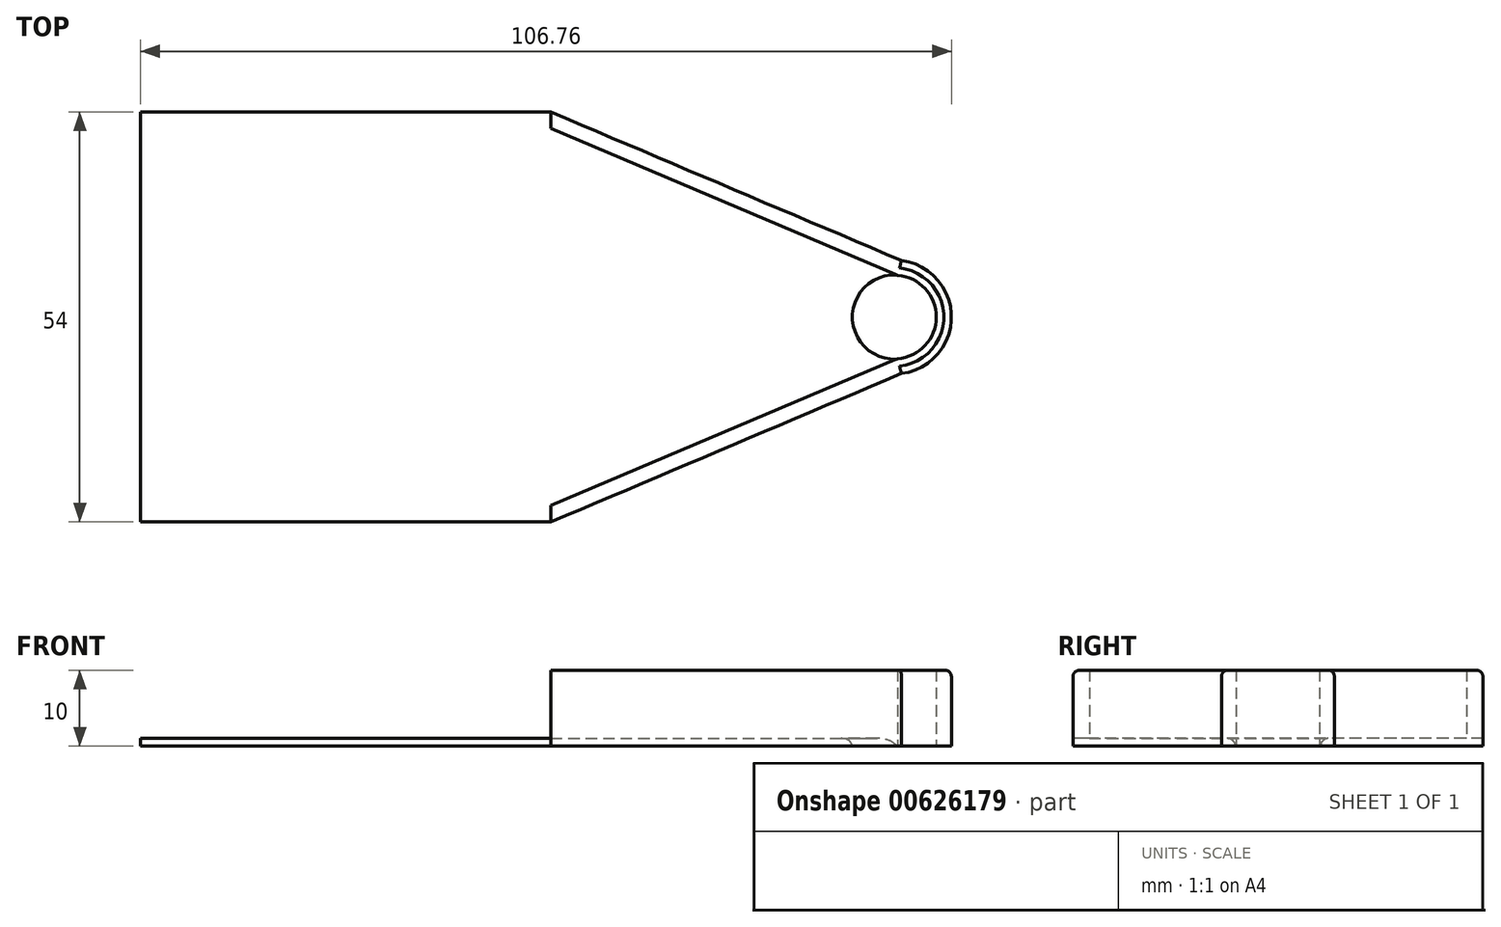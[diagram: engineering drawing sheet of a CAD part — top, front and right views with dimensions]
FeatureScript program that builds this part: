
annotation { "Feature Type Name" : "Feature", "Feature Type Description" : "" }
export const myFeature = defineFeature(function(context is Context, id is Id, definition is map)
    precondition{}
    {
        {
            var Q0;
            Q0=qCreatedBy(makeId("Top.planeOp"),FACE);
            var sketch = newSketch(context, id + "F0", { "sketchPlane" : qUnion([Q0])});
            skArc(sketch, "E0", {"start": v(12.3, -13.43) * mm, "mid": v(17.4, -7.95) * mm, "end": v(12.31, -2.46) * mm});
            skArc(sketch, "E1.3", {"start": v(12.81, -15.38) * mm, "mid": v(19.4, -7.94) * mm, "end": v(12.81, -0.5) * mm});
            skCircle(sketch, "E2", {"center": v(11.9, -7.94) * mm, "radius": 5.5 * mm});
            skLineSegment(sketch, "E3", {"start": v(-33.37, 19.06) * mm, "end": v(12.81, -0.5) * mm});
            skLineSegment(sketch, "E4", {"start": v(-33.37, -34.94) * mm, "end": v(12.81, -15.38) * mm});
            skLineSegment(sketch, "E5.0", {"start": v(-31.37, 16.04) * mm, "end": v(12.03, -2.34) * mm});
            skLineSegment(sketch, "E5.1", {"start": v(-31.37, -7.94) * mm, "end": v(-31.37, 16.04) * mm});
            skLineSegment(sketch, "E5.2", {"start": v(-31.37, -7.94) * mm, "end": v(-31.37, -31.92) * mm});
            skLineSegment(sketch, "E5.3", {"start": v(-31.37, -31.92) * mm, "end": v(12.03, -13.54) * mm});
            skLineSegment(sketch, "E6", {"start": v(12.03, -2.34) * mm, "end": v(12.31, -2.46) * mm});
            skLineSegment(sketch, "E7", {"start": v(12.03, -13.54) * mm, "end": v(12.3, -13.43) * mm});
            skLineSegment(sketch, "E8", {"start": v(-33.37, 19.06) * mm, "end": v(-33.37, -34.94) * mm});
            skLineSegment(sketch, "E9", {"start": v(-31.37, 16.04) * mm, "end": v(-33.37, 16.89) * mm});
            skLineSegment(sketch, "E10", {"start": v(-31.37, -31.92) * mm, "end": v(-33.37, -32.77) * mm});
            skLineSegment(sketch, "E11.bottom", {"start": v(-33.37, 19.06) * mm, "end": v(-87.37, 19.06) * mm});
            skLineSegment(sketch, "E11.top", {"start": v(-33.37, -34.94) * mm, "end": v(-87.37, -34.94) * mm});
            skLineSegment(sketch, "E11.right", {"start": v(-87.37, 19.06) * mm, "end": v(-87.37, -34.94) * mm});
            skSolve(sketch);
        }
        {
            var Q0;
            Q0=makeQuery(id+"F0.imprint","IMPRINT",FACE,{"disambiguationData":[TD([[makeQuery(id+"F0.imprint","IMPRINT",EDGE,{"derivedFrom":sQuery(id+"F0.wireOp",EDGE,"E5.0")}),-1.0]])]});
            var Q1;
            Q1=makeQuery(id+"F0.imprint","IMPRINT",FACE,{"disambiguationData":[TD([[makeQuery(id+"F0.imprint","IMPRINT",EDGE,{"derivedFrom":sQuery(id+"F0.wireOp",EDGE,"E5.1")}),1.0]])]});
            extrude(context, id + "F1", {"entities" : qUnion([Q0, Q1]), "depth" : 1 * mm, "offsetDistance" : 25 * mm});
        }
        {
            var Q0;
            Q0=makeQuery(id+"F0.imprint","IMPRINT",FACE,{"disambiguationData":[TD([[makeQuery(id+"F0.imprint","IMPRINT",EDGE,{"derivedFrom":sQuery(id+"F0.wireOp",EDGE,"E1.3")}),1.0]])]});
            extrude(context, id + "F2", {"entities" : qUnion([Q0]), "operationType" : NewBodyOperationType.ADD, "depth" : 10 * mm, "offsetDistance" : 25 * mm});
        }
        {
            var Q0;
            Q0 = qSketchRegion(id + "F0", true);
            extrude(context, id + "F3", {"entities" : qUnion([Q0]), "operationType" : NewBodyOperationType.ADD, "depth" : 1 * mm, "offsetDistance" : 25 * mm});
        }
        {
            var Q0;
            Q0=makeQuery(id+"F1.opExtrude","CAP_EDGE",EDGE,{"disambiguationData":[OSD([sQuery(id+"F0.wireOp",EDGE,"E2")])],"isStart":false});
            fillet(context, id + "F4", {"entities" : qUnion([Q0]), "radius" : 1.5 * mm, "rho" : 0.5, "crossSection" : FilletCrossSection.CONIC, "allowEdgeOverflow" : false});
        }
        {
            var Q0;
            Q0=makeQuery(id+"F2.opExtrude","CAP_EDGE",EDGE,{"disambiguationData":[OSD([sQuery(id+"F0.wireOp",EDGE,"E4")])],"isStart":false});
            var Q1;
            Q1=makeQuery(id+"F2.opExtrude","CAP_EDGE",EDGE,{"disambiguationData":[OSD([sQuery(id+"F0.wireOp",EDGE,"E1.3")])],"isStart":false});
            var Q2;
            Q2=makeQuery(id+"F2.opExtrude","CAP_EDGE",EDGE,{"disambiguationData":[OSD([sQuery(id+"F0.wireOp",EDGE,"E3")])],"isStart":false});
            fillet(context, id + "F5", {"entities" : qUnion([Q0, Q1, Q2]), "radius" : 1 * mm, "rho" : 0.5, "crossSection" : FilletCrossSection.CONIC, "allowEdgeOverflow" : false});
        }
    });
